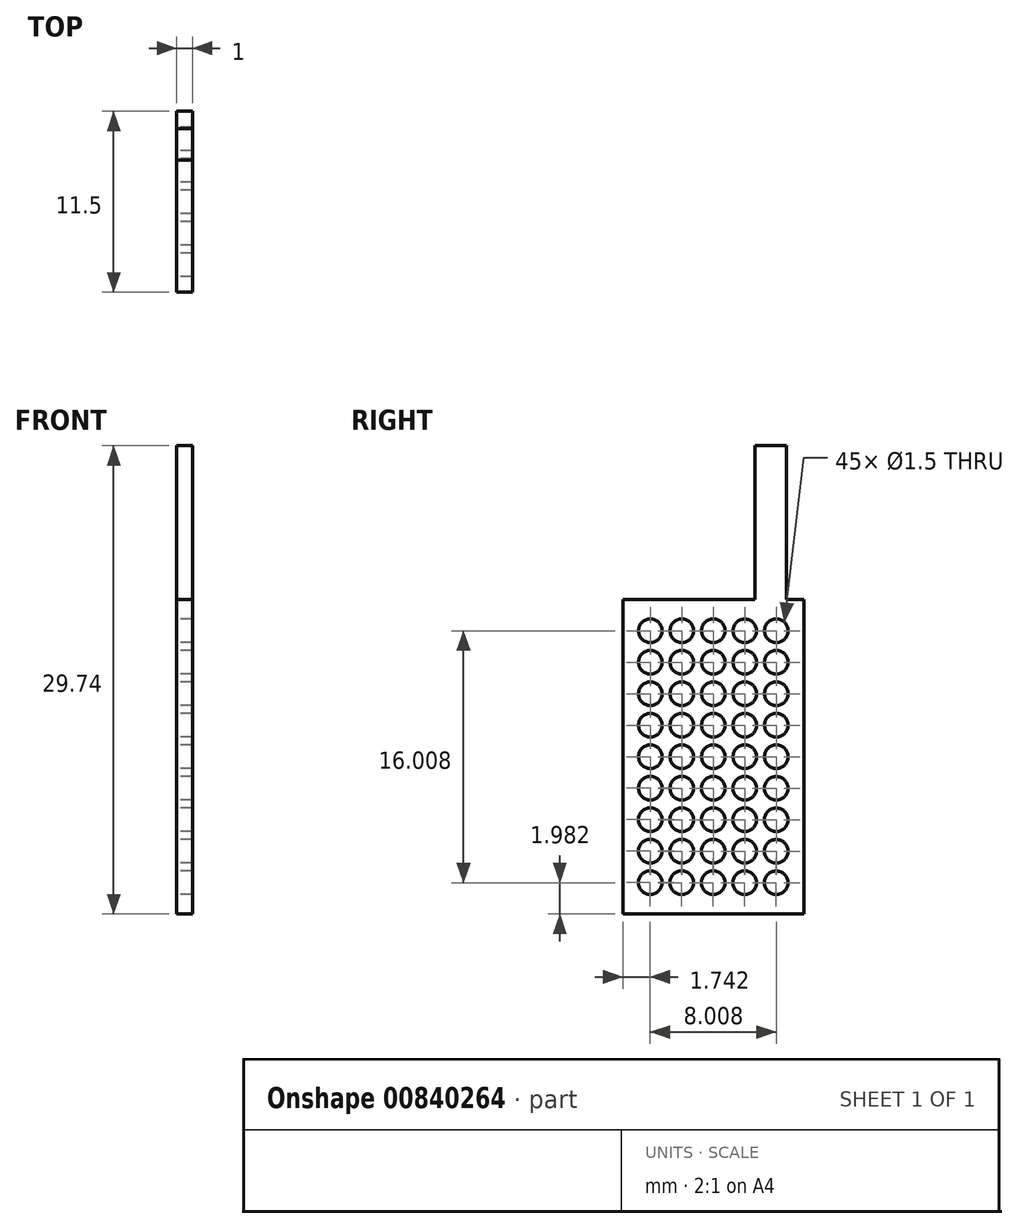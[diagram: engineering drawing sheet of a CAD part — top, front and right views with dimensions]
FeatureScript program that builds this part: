
annotation { "Feature Type Name" : "Feature", "Feature Type Description" : "" }
export const myFeature = defineFeature(function(context is Context, id is Id, definition is map)
    precondition{}
    {
        {
            var Q0;
            Q0=qCreatedBy(makeId("Right.planeOp"),FACE);
            var sketch = newSketch(context, id + "F0", { "sketchPlane" : qUnion([Q0])});
            skLineSegment(sketch, "E0.left", {"start": v(0, 0) * mm, "end": v(0, -19.74) * mm});
            skCircle(sketch, "E1", {"center": v(5.75, -5.75) * mm, "radius": 0.75 * mm});
            skLineSegment(sketch, "E2", {"start": v(11.5, 0) * mm, "end": v(11.5, -19.74) * mm});
            skLineSegment(sketch, "E3", {"start": v(10.38, 0.25) * mm, "end": v(10.38, 10) * mm});
            skLineSegment(sketch, "E4", {"start": v(10.38, 10) * mm, "end": v(8.38, 10) * mm});
            skLineSegment(sketch, "E5", {"start": v(8.38, 10) * mm, "end": v(8.38, 0.25) * mm});
            skCircle(sketch, "E6", {"center": v(5.75, -3.75) * mm, "radius": 0.75 * mm});
            skCircle(sketch, "E7", {"center": v(5.75, -1.75) * mm, "radius": 0.75 * mm});
            skCircle(sketch, "E8", {"center": v(3.75, -5.75) * mm, "radius": 0.75 * mm});
            skCircle(sketch, "E9", {"center": v(1.75, -5.75) * mm, "radius": 0.75 * mm});
            skCircle(sketch, "E10.MirrorC", {"center": v(1.75, -1.75) * mm, "radius": 0.75 * mm});
            skCircle(sketch, "E11.MirrorC", {"center": v(3.75, -1.75) * mm, "radius": 0.75 * mm});
            skCircle(sketch, "E12.MirrorC", {"center": v(1.75, -3.75) * mm, "radius": 0.75 * mm});
            skCircle(sketch, "E13", {"center": v(3.75, -3.75) * mm, "radius": 0.75 * mm});
            skCircle(sketch, "E14.MirrorC", {"center": v(7.75, -1.76) * mm, "radius": 0.75 * mm});
            skCircle(sketch, "E15.MirrorC", {"center": v(9.75, -1.75) * mm, "radius": 0.75 * mm});
            skCircle(sketch, "E16.MirrorC", {"center": v(9.75, -3.75) * mm, "radius": 0.75 * mm});
            skCircle(sketch, "E17.MirrorC", {"center": v(7.75, -3.75) * mm, "radius": 0.75 * mm});
            skCircle(sketch, "E18.MirrorC", {"center": v(7.75, -5.75) * mm, "radius": 0.75 * mm});
            skCircle(sketch, "E19.MirrorC", {"center": v(9.75, -5.75) * mm, "radius": 0.75 * mm});
            skCircle(sketch, "E20.MirrorC", {"center": v(1.75, -9.75) * mm, "radius": 0.75 * mm});
            skCircle(sketch, "E21.MirrorC", {"center": v(1.75, -7.75) * mm, "radius": 0.75 * mm});
            skCircle(sketch, "E22.MirrorC", {"center": v(3.75, -7.75) * mm, "radius": 0.75 * mm});
            skCircle(sketch, "E23.MirrorC", {"center": v(3.75, -9.75) * mm, "radius": 0.75 * mm});
            skCircle(sketch, "E24.MirrorC", {"center": v(7.75, -9.75) * mm, "radius": 0.75 * mm});
            skCircle(sketch, "E25.MirrorC", {"center": v(7.75, -7.75) * mm, "radius": 0.75 * mm});
            skCircle(sketch, "E26.MirrorC", {"center": v(9.75, -9.75) * mm, "radius": 0.75 * mm});
            skCircle(sketch, "E27.MirrorC", {"center": v(9.75, -7.75) * mm, "radius": 0.75 * mm});
            skCircle(sketch, "E28.MirrorC", {"center": v(5.75, -7.75) * mm, "radius": 0.75 * mm});
            skCircle(sketch, "E29.MirrorC", {"center": v(5.75, -9.75) * mm, "radius": 0.75 * mm});
            skPoint(sketch, "E30.endSnap0", {"position": v(11.5, -10) * mm});
            skCircle(sketch, "E31.MirrorC", {"center": v(1.75, -11.75) * mm, "radius": 0.75 * mm});
            skCircle(sketch, "E32.MirrorC", {"center": v(3.75, -11.75) * mm, "radius": 0.75 * mm});
            skCircle(sketch, "E33.MirrorC", {"center": v(5.75, -11.75) * mm, "radius": 0.75 * mm});
            skCircle(sketch, "E34.MirrorC", {"center": v(7.75, -11.76) * mm, "radius": 0.75 * mm});
            skCircle(sketch, "E35.MirrorC", {"center": v(9.75, -11.76) * mm, "radius": 0.75 * mm});
            skCircle(sketch, "E36.MirrorC", {"center": v(1.75, -13.75) * mm, "radius": 0.75 * mm});
            skCircle(sketch, "E37.MirrorC", {"center": v(3.75, -13.75) * mm, "radius": 0.75 * mm});
            skCircle(sketch, "E38.MirrorC", {"center": v(5.75, -13.75) * mm, "radius": 0.75 * mm});
            skCircle(sketch, "E39.MirrorC", {"center": v(7.75, -13.76) * mm, "radius": 0.75 * mm});
            skCircle(sketch, "E40.MirrorC", {"center": v(9.75, -13.76) * mm, "radius": 0.75 * mm});
            skCircle(sketch, "E41.MirrorC", {"center": v(1.74, -15.75) * mm, "radius": 0.75 * mm});
            skCircle(sketch, "E42.MirrorC", {"center": v(3.74, -15.75) * mm, "radius": 0.75 * mm});
            skCircle(sketch, "E43.MirrorC", {"center": v(5.74, -15.75) * mm, "radius": 0.75 * mm});
            skCircle(sketch, "E44.MirrorC", {"center": v(7.74, -15.76) * mm, "radius": 0.75 * mm});
            skCircle(sketch, "E45.MirrorC", {"center": v(9.74, -15.76) * mm, "radius": 0.75 * mm});
            skCircle(sketch, "E46.MirrorC", {"center": v(9.74, -17.76) * mm, "radius": 0.75 * mm});
            skCircle(sketch, "E47.MirrorC", {"center": v(7.74, -17.76) * mm, "radius": 0.75 * mm});
            skCircle(sketch, "E48.MirrorC", {"center": v(5.74, -17.75) * mm, "radius": 0.75 * mm});
            skCircle(sketch, "E49.MirrorC", {"center": v(3.74, -17.75) * mm, "radius": 0.75 * mm});
            skCircle(sketch, "E50.MirrorC", {"center": v(1.74, -17.75) * mm, "radius": 0.75 * mm});
            skLineSegment(sketch, "E51.0", {"start": v(1.75, 0.25) * mm, "end": v(11.5, 0.25) * mm});
            skLineSegment(sketch, "E52.0", {"start": v(11.5, -19.74) * mm, "end": v(0, -19.74) * mm});
            skPoint(sketch, "E53.orphan", {"position": v(11.5, -20) * mm});
            skLineSegment(sketch, "E54", {"start": v(11.5, 0) * mm, "end": v(11.5, 0.25) * mm});
            skLineSegment(sketch, "E55", {"start": v(1.75, 0.25) * mm, "end": v(0, 0.25) * mm});
            skLineSegment(sketch, "E56", {"start": v(0, 0.25) * mm, "end": v(0, 0) * mm});
            skPoint(sketch, "E57.orphan", {"position": v(8.38, 0) * mm});
            skSolve(sketch);
        }
        {
            var Q0;
            Q0=makeQuery(id+"F0.imprint","IMPRINT",FACE,{"disambiguationData":[TD([[makeQuery(id+"F0.imprint","IMPRINT",EDGE,{"derivedFrom":sQuery(id+"F0.wireOp",EDGE,"E0.bottom")}),-1.0]])]});
            var Q1;
            Q1=makeQuery(id+"F0.imprint","IMPRINT",FACE,{"disambiguationData":[TD([[makeQuery(id+"F0.imprint","IMPRINT",EDGE,{"derivedFrom":sQuery(id+"F0.wireOp",EDGE,"r65wuaeR-pUGk-UfhY-v5oq-7bkjaNJfQmKm.bottom")}),-1.0]])]});
            var Q2;
            Q2=makeQuery(id+"F0.imprint","IMPRINT",FACE,{"disambiguationData":[TD([[makeQuery(id+"F0.imprint","IMPRINT",EDGE,{"derivedFrom":sQuery(id+"F0.wireOp",EDGE,"n5EaUuf3-CoM6-EQkv-XzT1-ydr3onYee1LO.bottom")}),1.0]])]});
            var Q3;
            Q3=makeQuery(id+"F0.imprint","IMPRINT",FACE,{"disambiguationData":[TD([[makeQuery(id+"F0.imprint","IMPRINT",EDGE,{"derivedFrom":sQuery(id+"F0.wireOp",EDGE,"2NUbogVr-x7fL-9LVX-WR3f-6RiyyzUn8nbi.bottom")}),-1.0]])]});
            var Q4;
            Q4=makeQuery(id+"F0.imprint","IMPRINT",FACE,{"disambiguationData":[TD([[makeQuery(id+"F0.imprint","IMPRINT",EDGE,{"derivedFrom":sQuery(id+"F0.wireOp",EDGE,"E0.left")}),1.0]])]});
            var Q5;
            {var subQ0=sQuery(id+"F0.wireOp",EDGE,"E3");Q5=makeQuery(id+"F0.imprint","IMPRINT",FACE,{"disambiguationData":[TD([[makeQuery(id+"F0.imprint","IMPRINT",EDGE,{"derivedFrom":subQ0}),1.0]])]});}
            extrude(context, id + "F1", {"entities" : qUnion([Q0, Q1, Q2, Q3, Q4, Q5]), "depth" : 1 * mm, "offsetDistance" : 25 * mm});
        }
    });
